# Revit family: Sanitary_Toilet-Seats_DURAVIT-AG_ME-by-Starck-Toilet-seat-374x458x56-mm-002001
name_source: partatom
category: Specialty Equipment
revit_build: Autodesk Revit 2018 (Build: 20180329_1100(x64)
units: mm (PartAtom-declared; Revit-internal decimal feet)

## family parameters
Always vertical = No
Cut with Voids When Loaded = No
OmniClass Number = 23.31.19.19.17
OmniClass Title = Water Closet Seats
Part Type = Normal
Room Calculation Point = No
Round Connector Dimension = Use Diameter
Shared = No
Work Plane-Based = Yes

## types (2) — shared parameters
BIMobject category = Toilet Seats
Default Elevation = 1219.2 mm  [stored 4 ft]
Design country = Germany
Details material = Duravit - Metal - Stainless Steel
ETIM classification = EC011196 | Toilet seat
Edition number = 1
IFC Classification = Furnishing Element
Installation instructions = http://pro.duravit.com
Manufacturer = Duravit
Manufacturer name = DURAVIT AG
Masterformat 2014 Code = 22 41 13.13
Masterformat 2014 Description = Residential Water Closets
Material main = Duroplast
Model = ME by Starck Toilet seat 374x458x56 mm - 002001
OmniClass Code = 23-31 19 19 17
OmniClass Description = Water Closet Seats
Product Guid = d580ed83-4f62-4995-8d19-686474a6c55c
Product SKU = ME-by-Starck-Toilet-seat-374x458x56-mm-002001
Product certification = http://pro.duravit.com
Product data url = https://bimobject.com
Product family = ME by Starck
Product group = Toilet seat
Product name = ME by Starck Toilet seat 374x458x56 mm - 002001
Product url = http://pro.duravit.com
QR code = https://bimobject.com
Technical description = http://pro.duravit.com
UNSPSC Code = 301815
URL = https://www.duravit.com
Uniclass 2015 Code = Pr_40_20_93_95
Uniclass 2015 Name = WC seats and covers
Uniformat II Code = E2010
Uniformat II Description = Fixed Furnishings
Weight Net (Kg) = 2,29
Youtube clip = http://pro.duravit.com

## per-type parameters (varying)
| type | Description | Main material |
| 00 - White Alpin | Duravit ME by Starck Toilet seat White 374x458x56 mm - 0020010000 | Duravit - Plastic - 00 - White Alpin |
| 32 - White Satin Matt | Duravit ME by Starck Toilet seat White Satin Matt 374x458x56 mm - 0020012600 | Duravit - Plastic - 32 - White Satin Matt |

note: [stored X ft] marks values corroborated as IEEE doubles in the binary element streams (Revit-internal decimal feet)

## geometry (parser evidence)
native form markers: Sweep x3
no freeform markers — native parametric forms only
